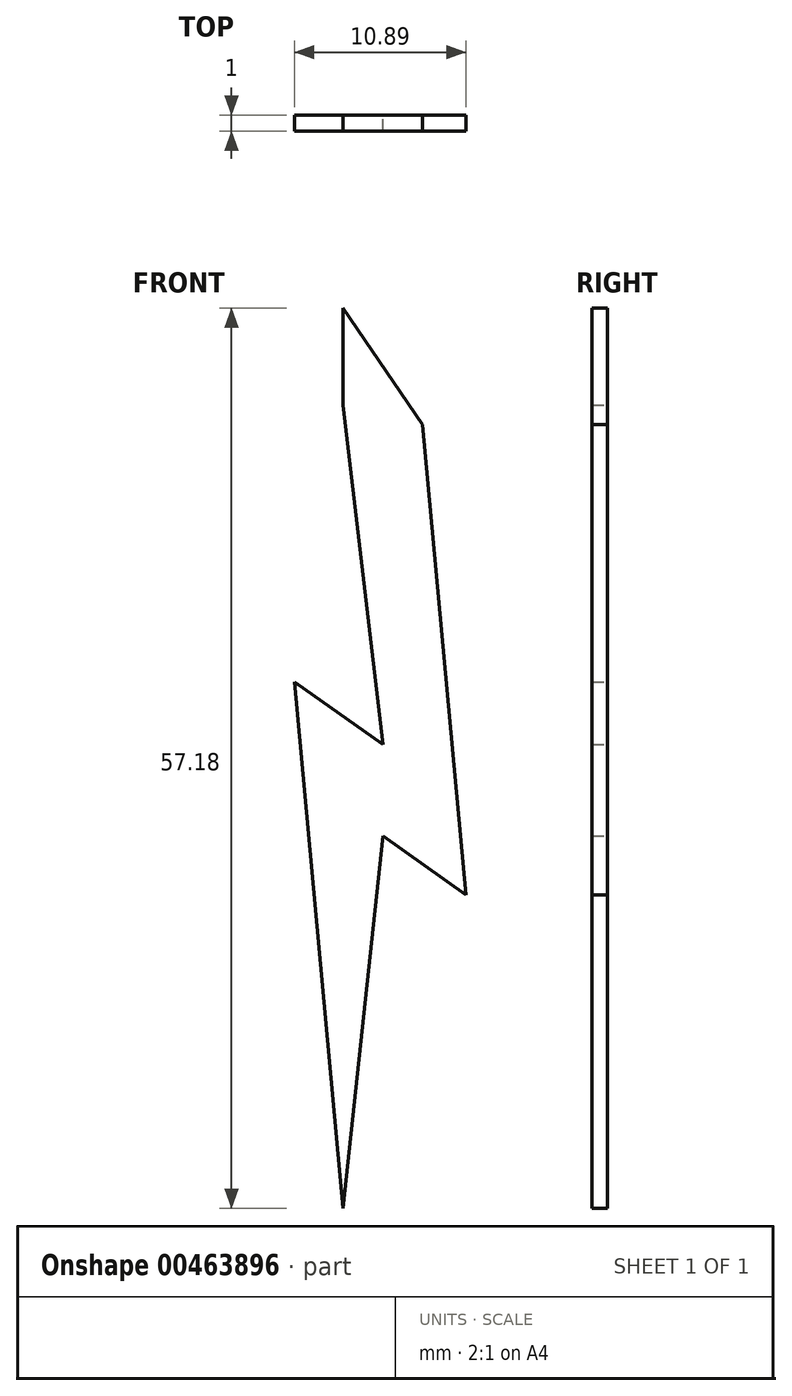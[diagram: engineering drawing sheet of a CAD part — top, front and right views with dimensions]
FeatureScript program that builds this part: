
annotation { "Feature Type Name" : "Feature", "Feature Type Description" : "" }
export const myFeature = defineFeature(function(context is Context, id is Id, definition is map)
    precondition{}
    {
        {
            var Q0;
            Q0=qCreatedBy(makeId("Front.planeOp"),FACE);
            var sketch = newSketch(context, id + "F0", { "sketchPlane" : qUnion([Q0])});
            skLineSegment(sketch, "E0", {"start": v(0, 0) * mm, "end": v(-3.08, 33.44) * mm});
            skLineSegment(sketch, "E1", {"start": v(-3.08, 33.44) * mm, "end": v(2.54, 29.45) * mm});
            skLineSegment(sketch, "E2", {"start": v(0, 51.02) * mm, "end": v(2.54, 29.45) * mm});
            skLineSegment(sketch, "E3", {"start": v(0, 0) * mm, "end": v(2.54, 23.65) * mm});
            skLineSegment(sketch, "E4", {"start": v(2.54, 23.65) * mm, "end": v(7.81, 19.9) * mm});
            skLineSegment(sketch, "E5", {"start": v(7.81, 19.9) * mm, "end": v(5.06, 49.78) * mm});
            skLineSegment(sketch, "E6", {"start": v(0, 51.02) * mm, "end": v(0, 57.18) * mm});
            skLineSegment(sketch, "E7", {"start": v(5.06, 49.78) * mm, "end": v(0, 57.18) * mm});
            skSolve(sketch);
        }
        {
            var Q0;
            Q0=makeQuery(id+"F0.imprint","IMPRINT",FACE,{"disambiguationData":[TD([[makeQuery(id+"F0.imprint","IMPRINT",EDGE,{"derivedFrom":sQuery(id+"F0.wireOp",EDGE,"E0")}),-1.0]])]});
            extrude(context, id + "F1", {"entities" : qUnion([Q0]), "depth" : 1 * mm});
        }
    });
